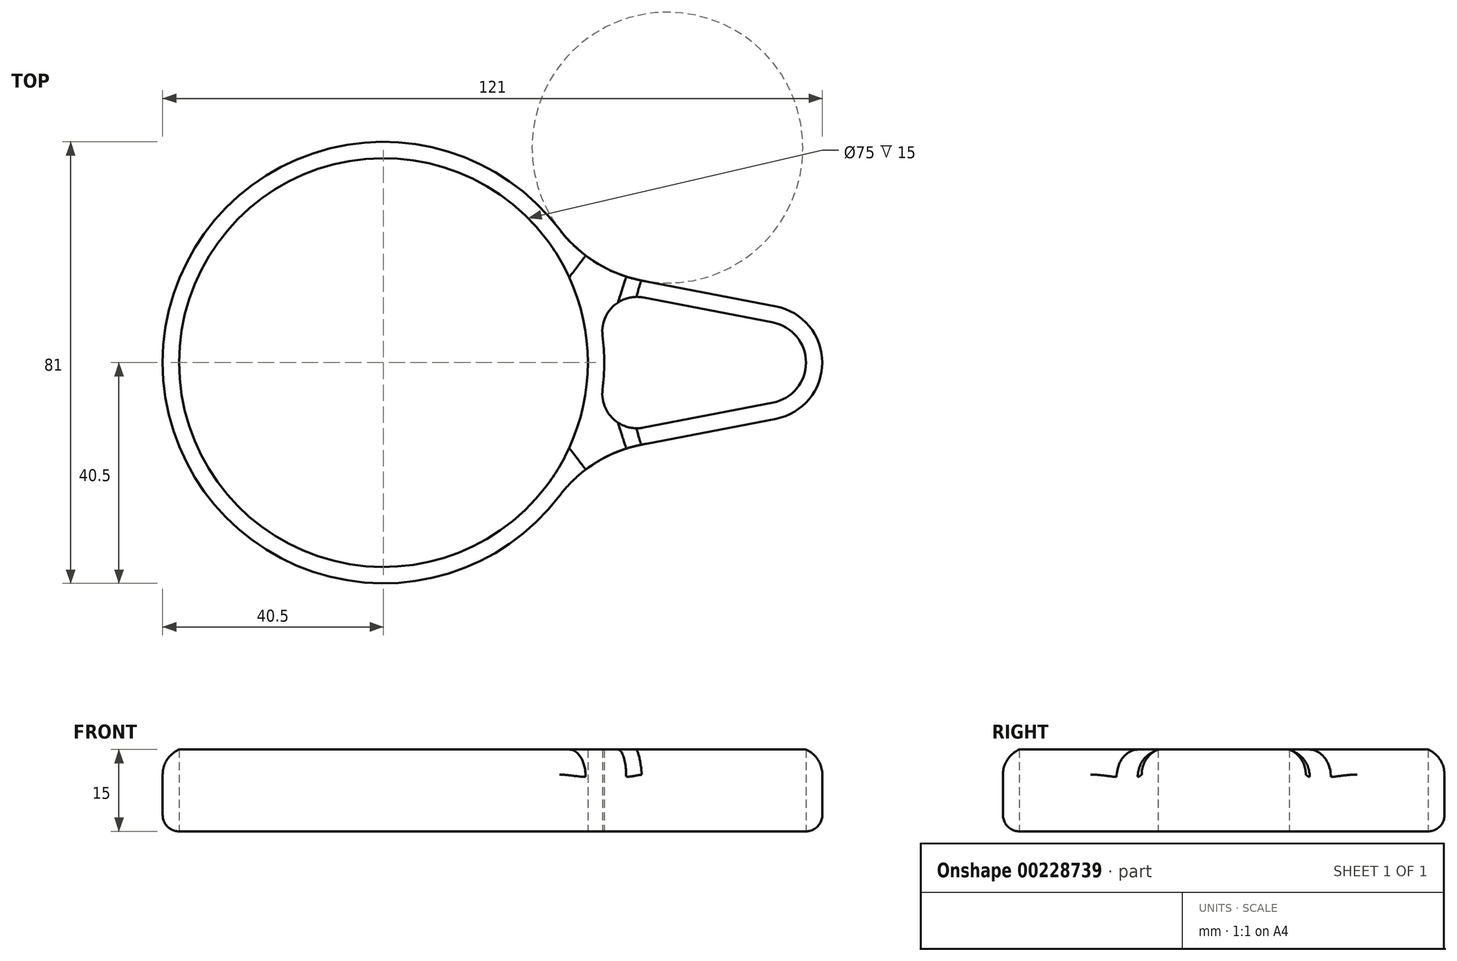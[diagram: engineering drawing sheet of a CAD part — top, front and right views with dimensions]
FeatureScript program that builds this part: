
annotation { "Feature Type Name" : "Feature", "Feature Type Description" : "" }
export const myFeature = defineFeature(function(context is Context, id is Id, definition is map)
    precondition{}
    {
        {
            var Q0;
            Q0=qCreatedBy(makeId("Top.planeOp"),FACE);
            var sketch = newSketch(context, id + "F0", { "sketchPlane" : qUnion([Q0])});
            skCircle(sketch, "E0", {"center": v(0, 0) * mm, "radius": 37.5 * mm});
            skCircle(sketch, "E1", {"center": v(0, 0) * mm, "radius": 40.5 * mm});
            skLineSegment(sketch, "E2", {"start": v(0, 0) * mm, "end": v(70, 0) * mm, "construction": true});
            skArc(sketch, "E3", {"start": v(71.99, -10.31) * mm, "mid": v(80.5, 0) * mm, "end": v(71.99, 10.31) * mm});
            skLineSegment(sketch, "E4", {"start": v(71.99, -10.31) * mm, "end": v(47.4, -15.05) * mm});
            skLineSegment(sketch, "E5.MirrorCS", {"start": v(71.99, 10.31) * mm, "end": v(47.4, 15.05) * mm});
            skLineSegment(sketch, "E6", {"start": v(40.5, 0) * mm, "end": v(51.5, 0) * mm});
            skCircle(sketch, "E7", {"center": v(51.5, 0) * mm, "radius": 11 * mm, "construction": true});
            skArc(sketch, "E8", {"start": v(47.4, -15.05) * mm, "mid": v(38.97, -18.35) * mm, "end": v(32.29, -24.45) * mm});
            skArc(sketch, "E9.MirrorCS", {"start": v(47.4, 15.05) * mm, "mid": v(38.97, 18.35) * mm, "end": v(32.29, 24.45) * mm});
            skCircle(sketch, "E10", {"center": v(70, 0) * mm, "radius": 7.5 * mm, "construction": true});
            skLineSegment(sketch, "E11", {"start": v(71.42, -7.36) * mm, "end": v(47.68, -11.94) * mm});
            skArc(sketch, "E12", {"start": v(47.68, -11.94) * mm, "mid": v(42.16, -10.35) * mm, "end": v(40.2, -4.95) * mm});
            skLineSegment(sketch, "E13", {"start": v(70, 0) * mm, "end": v(77.5, 0) * mm, "construction": true});
            skArc(sketch, "E14", {"start": v(71.42, -7.36) * mm, "mid": v(75.78, -4.78) * mm, "end": v(77.5, 0) * mm});
            skLineSegment(sketch, "E15.MirrorCS", {"start": v(71.42, 7.36) * mm, "end": v(47.68, 11.94) * mm});
            skArc(sketch, "E16.MirrorCS", {"start": v(47.68, 11.94) * mm, "mid": v(42.16, 10.35) * mm, "end": v(40.2, 4.95) * mm});
            skArc(sketch, "E17.MirrorCS", {"start": v(71.42, 7.36) * mm, "mid": v(75.78, 4.78) * mm, "end": v(77.5, 0) * mm});
            skSolve(sketch);
        }
        {
            var Q0;
            Q0=qSketchRegion(id+"F0",true);
            extrude(context, id + "F1", {"entities" : qUnion([Q0]), "depth" : 12 * mm, "hasSecondDirection" : true, "secondDirectionOppositeDirection" : true, "secondDirectionDepth" : 3 * mm});
        }
        {
            var Q0;
            Q0=makeQuery(id+"F1.opExtrude","CAP_EDGE",EDGE,{"disambiguationData":[OSD([sQuery(id+"F0.wireOp",EDGE,"E4")])],"isStart":true});
            var Q1;
            {var subQ0=sQuery(id+"F0.wireOp",EDGE,"E1");Q1=makeQuery(id+"F1.opExtrude","CAP_EDGE",EDGE,{"disambiguationData":[OSD([subQ0]),TDD([makeQuery(id+"F0.imprint","IMPRINT",EDGE,{"disambiguationData":[TD([[makeQuery(id+"F0.imprint","INTERSECT",VERTEX,{"derivedFrom":[subQ0,sQuery(id+"F0.wireOp",EDGE,"49ead12a-8969-4f14-99cd-0dc1652e97c1")]}),1.0]])],"derivedFrom":subQ0})])],"isStart":true});}
            fillet(context, id + "F2", {"entities" : qUnion([Q0, Q1]), "radius" : 3 * mm, "tangentPropagation" : true, "allowEdgeOverflow" : false});
        }
        {
            var Q0;
            Q0=makeQuery(id+"F1.opExtrude","CAP_EDGE",EDGE,{"disambiguationData":[OSD([sQuery(id+"F0.wireOp",EDGE,"E3")])],"isStart":false});
            var Q1;
            Q1=makeQuery(id+"F1.opExtrude","CAP_EDGE",EDGE,{"disambiguationData":[OSD([sQuery(id+"F0.wireOp",EDGE,"E5.MirrorCS")])],"isStart":false});
            var Q2;
            Q2=makeQuery(id+"F1.opExtrude","CAP_EDGE",EDGE,{"disambiguationData":[OSD([sQuery(id+"F0.wireOp",EDGE,"E4")])],"isStart":false});
            var Q3;
            Q3=makeQuery(id+"F1.opExtrude","CAP_EDGE",EDGE,{"disambiguationData":[OSD([sQuery(id+"F0.wireOp",EDGE,"E9.MirrorCS")])],"isStart":false});
            var Q4;
            Q4=makeQuery(id+"F1.opExtrude","CAP_EDGE",EDGE,{"disambiguationData":[OSD([sQuery(id+"F0.wireOp",EDGE,"E8")])],"isStart":false});
            fillet(context, id + "F3", {"entities" : qUnion([Q0, Q1, Q2, Q3, Q4]), "radius" : 5 * mm, "tangentPropagation" : true, "allowEdgeOverflow" : false});
        }
    });
